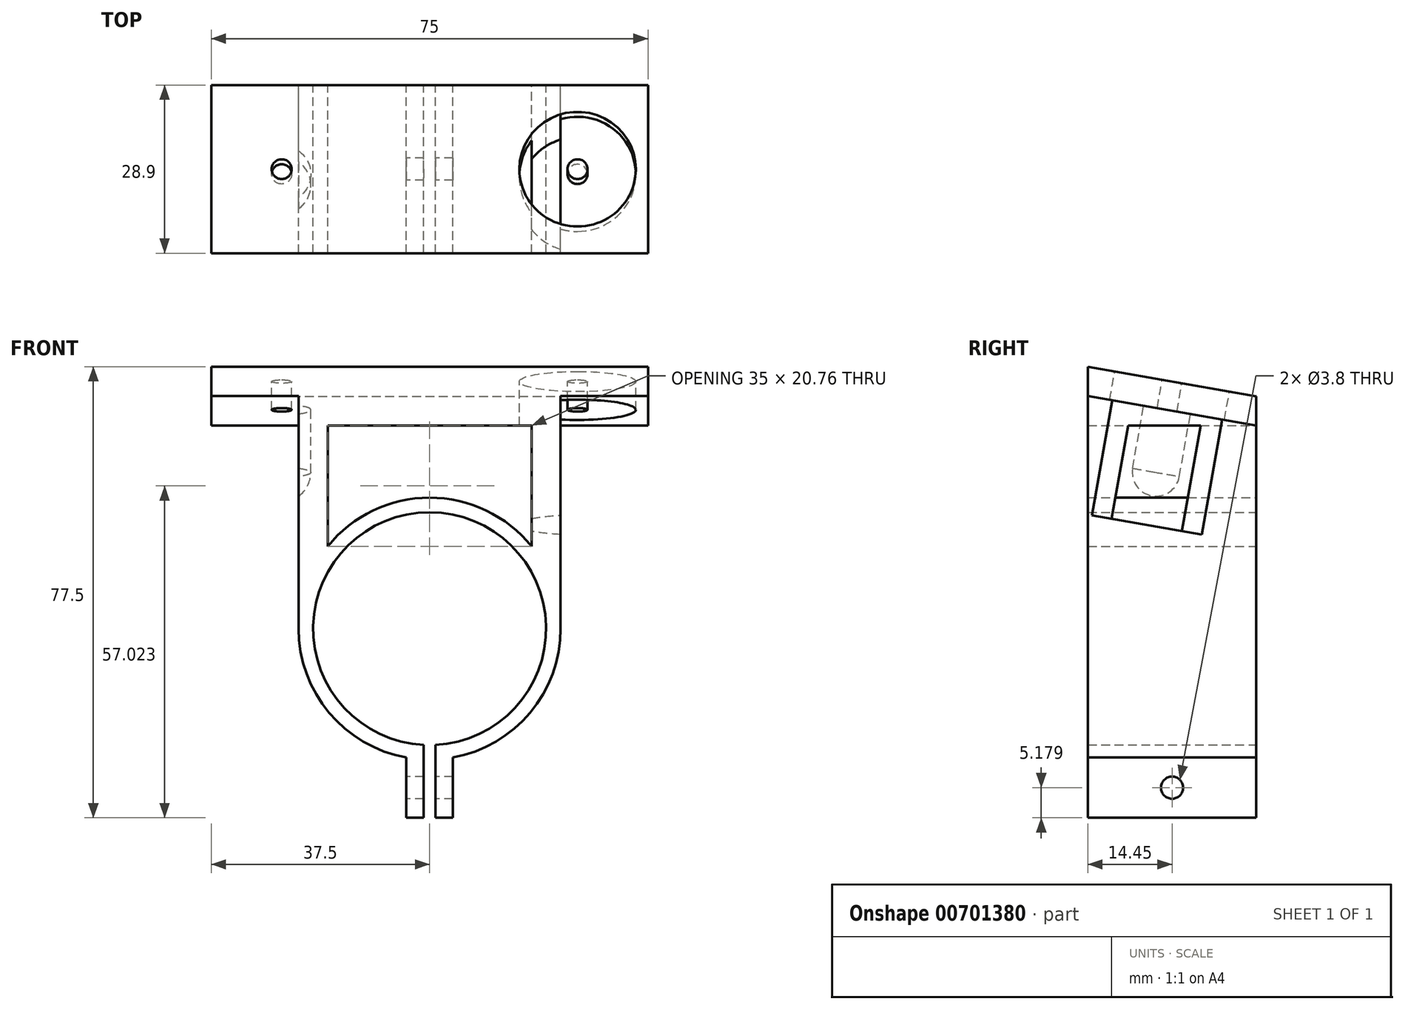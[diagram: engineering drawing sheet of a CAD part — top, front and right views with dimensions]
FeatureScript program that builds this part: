
annotation { "Feature Type Name" : "Feature", "Feature Type Description" : "" }
export const myFeature = defineFeature(function(context is Context, id is Id, definition is map)
    precondition{}
    {
        {
            var Q0;
            Q0=qCreatedBy(makeId("Front.planeOp"),FACE);
            var sketch = newSketch(context, id + "F0", { "sketchPlane" : qUnion([Q0])});
            skCircle(sketch, "E0", {"center": v(0, 0) * mm, "radius": 22.5 * mm});
            skLineSegment(sketch, "E1", {"start": v(-22.5, 0) * mm, "end": v(-22.5, 45) * mm});
            skLineSegment(sketch, "E2", {"start": v(22.5, 0) * mm, "end": v(22.5, 45) * mm});
            skLineSegment(sketch, "E3", {"start": v(22.5, 45) * mm, "end": v(-22.5, 45) * mm});
            skPoint(sketch, "E4", {"position": v(0, -22.5) * mm});
            skSolve(sketch);
        }
        {
            var Q0;
            Q0=makeQuery(id+"F0.imprint","IMPRINT",FACE,{"disambiguationData":[TD([[makeQuery(id+"F0.imprint","IMPRINT",EDGE,{"derivedFrom":sQuery(id+"F0.wireOp",EDGE,"E0")}),1.0]])]});
            var Q1;
            {var subQ0=sQuery(id+"F0.wireOp",EDGE,"E1");Q1=makeQuery(id+"F0.imprint","IMPRINT",FACE,{"disambiguationData":[TD([[makeQuery(id+"F0.imprint","IMPRINT",EDGE,{"derivedFrom":subQ0}),-1.0]])]});}
            extrude(context, id + "F1", {"entities" : qUnion([Q0, Q1]), "depth" : 28.9 * mm, "offsetDistance" : 25 * mm});
        }
        {
            var Q0;
            Q0=sQuery(id+"F0.wireOp",VERTEX,"E0.center");
            var Q1;
            Q1=makeQuery(id+"F1.opExtrude","SWEPT_BODY",BODY,{"disambiguationData":[OSD([sQuery(id+"F0.wireOp",EDGE,"E0")])]});
            hole(context, id + "F2", {"style" : HoleStyle.SIMPLE, "endStyle" : HoleEndStyle.THROUGH, "oppositeDirection" : true, "holeDiameter" : 40 * mm, "majorDiameter" : 5 * mm, "isTappedThrough" : true, "tappedDepth" : 12 * mm, "tapClearance" : 3, "locations" : qUnion([Q0]), "scope" : qUnion([Q1])});
        }
        {
            var Q0;
            Q0=makeQuery(id+"F1.opExtrude","SWEPT_FACE",FACE,{"disambiguationData":[OSD([sQuery(id+"F0.wireOp",EDGE,"E2")])]});
            var sketch = newSketch(context, id + "F3", { "sketchPlane" : qUnion([Q0])});
            skLineSegment(sketch, "E5", {"start": v(-28.9, 45) * mm, "end": v(0, 39.9) * mm});
            skSolve(sketch);
        }
        {
            var Q0;
            {var subQ0=sQuery(id+"F3.wireOp",EDGE,"E5");Q0=makeQuery(id+"F3.imprint","IMPRINT",FACE,{"disambiguationData":[TD([[makeQuery(id+"F3.imprint","IMPRINT",EDGE,{"derivedFrom":subQ0}),1.0]])]});}
            extrude(context, id + "F4", {"entities" : qUnion([Q0]), "operationType" : NewBodyOperationType.REMOVE, "endBound" : BoundingType.THROUGH_ALL, "oppositeDirection" : true, "depth" : 25 * mm, "offsetDistance" : 25 * mm});
        }
        {
            var Q0;
            {var subQ0=sQuery(id+"F0.wireOp",EDGE,"E0");var subQ1=makeQuery(id+"F0.imprint","INTERSECT",VERTEX,{"derivedFrom":[subQ0,sQuery(id+"F0.wireOp",EDGE,"E1")]});Q0=makeQuery(id+"F0.imprint","IMPRINT",FACE,{"disambiguationData":[TD([[makeQuery(id+"F0.imprint","IMPRINT",EDGE,{"disambiguationData":[TD([[subQ1,1.0]])],"derivedFrom":subQ0}),1.0]])]});}
            var sketch = newSketch(context, id + "F5", { "sketchPlane" : qUnion([Q0])});
            skLineSegment(sketch, "E6", {"start": v(0, -24.67) * mm, "end": v(0, 0) * mm, "construction": true});
            skLineSegment(sketch, "E7", {"start": v(1, 7.5) * mm, "end": v(1, 0.8) * mm});
            skLineSegment(sketch, "E8.MirrorCS", {"start": v(-1, 7.5) * mm, "end": v(-1, 0.8) * mm});
            skLineSegment(sketch, "E9.bottom", {"start": v(1, 0.8) * mm, "end": v(-1, 0.8) * mm});
            skLineSegment(sketch, "E9.top", {"start": v(1, -32.5) * mm, "end": v(-1, -32.5) * mm});
            skLineSegment(sketch, "E9.left", {"start": v(1, 0.8) * mm, "end": v(1, -32.5) * mm});
            skLineSegment(sketch, "E9.right", {"start": v(-1, 0.8) * mm, "end": v(-1, -32.5) * mm});
            skLineSegment(sketch, "E10.bottom", {"start": v(-1, 7.5) * mm, "end": v(-4, 7.5) * mm});
            skLineSegment(sketch, "E10.top", {"start": v(-1, -32.5) * mm, "end": v(-4, -32.5) * mm});
            skLineSegment(sketch, "E10.left", {"start": v(-1, 7.5) * mm, "end": v(-1, -32.5) * mm});
            skLineSegment(sketch, "E10.right", {"start": v(-4, 7.5) * mm, "end": v(-4, -32.5) * mm});
            skLineSegment(sketch, "E11.MirrorCS", {"start": v(4, 7.5) * mm, "end": v(4, -32.5) * mm});
            skLineSegment(sketch, "E12.MirrorCS", {"start": v(1, 7.5) * mm, "end": v(4, 7.5) * mm});
            skLineSegment(sketch, "E13.MirrorCS", {"start": v(1, -32.5) * mm, "end": v(4, -32.5) * mm});
            skSolve(sketch);
        }
        {
            var Q0;
            {var subQ0=sQuery(id+"F5.wireOp",EDGE,"E13.MirrorCS");Q0=makeQuery(id+"F5.imprint","IMPRINT",FACE,{"disambiguationData":[TD([[makeQuery(id+"F5.imprint","IMPRINT",EDGE,{"derivedFrom":subQ0}),1.0]])]});}
            var Q1;
            {var subQ0=sQuery(id+"F5.wireOp",EDGE,"E10.top");Q1=makeQuery(id+"F5.imprint","IMPRINT",FACE,{"disambiguationData":[TD([[makeQuery(id+"F5.imprint","IMPRINT",EDGE,{"derivedFrom":subQ0}),-1.0]])]});}
            extrude(context, id + "F6", {"entities" : qUnion([Q0, Q1]), "operationType" : NewBodyOperationType.ADD, "depth" : 28.9 * mm, "offsetDistance" : 25 * mm});
        }
        {
            var Q0;
            {var subQ0=sQuery(id+"F5.wireOp",EDGE,"E9.bottom");Q0=makeQuery(id+"F5.imprint","IMPRINT",FACE,{"disambiguationData":[TD([[makeQuery(id+"F5.imprint","IMPRINT",EDGE,{"derivedFrom":subQ0}),1.0]])]});}
            extrude(context, id + "F7", {"entities" : qUnion([Q0]), "operationType" : NewBodyOperationType.REMOVE, "endBound" : BoundingType.THROUGH_ALL, "depth" : 25 * mm, "offsetDistance" : 25 * mm});
        }
        {
            var Q0;
            Q0=makeQuery(id+"F6.opExtrude","SWEPT_FACE",FACE,{"disambiguationData":[OSD([sQuery(id+"F5.wireOp",EDGE,"E10.right")])]});
            var sketch = newSketch(context, id + "F8", { "sketchPlane" : qUnion([Q0])});
            skLineSegment(sketch, "E14", {"start": v(14.45, -22.14) * mm, "end": v(14.45, -32.5) * mm, "construction": true});
            skCircle(sketch, "E15", {"center": v(14.45, -27.32) * mm, "radius": 1.9 * mm});
            skSolve(sketch);
        }
        {
            var Q0;
            Q0=makeQuery(id+"F8.imprint","IMPRINT",FACE,{"disambiguationData":[TD([[makeQuery(id+"F8.imprint","IMPRINT",EDGE,{"derivedFrom":sQuery(id+"F8.wireOp",EDGE,"E15")}),1.0]])]});
            extrude(context, id + "F9", {"entities" : qUnion([Q0]), "operationType" : NewBodyOperationType.REMOVE, "endBound" : BoundingType.THROUGH_ALL, "oppositeDirection" : true, "depth" : 25 * mm, "offsetDistance" : 25 * mm});
        }
        {
            var Q0;
            Q0=makeQuery(id+"F1.opExtrude","SWEPT_FACE",FACE,{"disambiguationData":[OSD([sQuery(id+"F0.wireOp",EDGE,"E1")])]});
            var sketch = newSketch(context, id + "F10", { "sketchPlane" : qUnion([Q0])});
            skLineSegment(sketch, "E16", {"start": v(0, 39.9) * mm, "end": v(28.9, 45) * mm});
            skLineSegment(sketch, "E17", {"start": v(28.9, 45) * mm, "end": v(28.9, 40) * mm});
            skLineSegment(sketch, "E18", {"start": v(0, 39.9) * mm, "end": v(0, 34.9) * mm});
            skLineSegment(sketch, "E19", {"start": v(28.9, 40) * mm, "end": v(0, 34.9) * mm});
            skSolve(sketch);
        }
        {
            var Q0;
            Q0=makeQuery(id+"F10.imprint","IMPRINT",FACE,{"disambiguationData":[TD([[makeQuery(id+"F10.imprint","IMPRINT",EDGE,{"derivedFrom":sQuery(id+"F10.wireOp",EDGE,"E16")}),-1.0]])]});
            extrude(context, id + "F11", {"entities" : qUnion([Q0]), "operationType" : NewBodyOperationType.ADD, "depth" : 15 * mm, "offsetDistance" : 25 * mm});
        }
        {
            var Q0;
            Q0=makeQuery(id+"F11.opExtrude","CAP_FACE",FACE,{"disambiguationData":[OSD([sQuery(id+"F10.wireOp",EDGE,"E16"),sQuery(id+"F10.wireOp",EDGE,"E17"),sQuery(id+"F10.wireOp",EDGE,"E18"),sQuery(id+"F10.wireOp",EDGE,"E19")])],"isStart":false});
            var sketch = newSketch(context, id + "F12", { "sketchPlane" : qUnion([Q0])});
            skSolve(sketch);
        }
        {
            var Q0;
            Q0=makeQuery(id+"F12.imprint","IMPRINT",FACE,{"disambiguationData":[TD([[makeQuery(id+"F12.imprint","IMPRINT",EDGE,{"derivedFrom":makeQuery(id+"F11.opExtrude","CAP_EDGE",EDGE,{"disambiguationData":[OSD([sQuery(id+"F10.wireOp",EDGE,"E16")])],"isStart":false})}),-1.0]])]});
            extrude(context, id + "F13", {"entities" : qUnion([Q0]), "operationType" : NewBodyOperationType.ADD, "oppositeDirection" : true, "depth" : 75 * mm, "offsetDistance" : 25 * mm});
        }
        {
            var Q0;
            {var subQ0=sQuery(id+"F10.wireOp",EDGE,"E16");Q0=makeQuery(id+"F13.boolean.opBoolean","MERGE",FACE,{"derivedFrom":[makeQuery(id+"F11.boolean.opBoolean","MERGE",FACE,{"derivedFrom":[makeQuery(id+"F4.boolean.opBoolean","COPY",FACE,{"derivedFrom":makeQuery(id+"F4.opExtrude","SWEPT_FACE",FACE,{"disambiguationData":[OSD([sQuery(id+"F3.wireOp",EDGE,"E5")])]})}),makeQuery(id+"F11.opExtrude","SWEPT_FACE",FACE,{"disambiguationData":[OSD([subQ0])]})]}),makeQuery(id+"F13.opExtrude","SWEPT_FACE",FACE,{"disambiguationData":[OSD([subQ0])]})]});}
            var sketch = newSketch(context, id + "F14", { "sketchPlane" : qUnion([Q0])});
            skLineSegment(sketch, "E20", {"start": v(37.5, -21.6) * mm, "end": v(-37.5, -21.6) * mm, "construction": true});
            skLineSegment(sketch, "E21", {"start": v(0, -6.93) * mm, "end": v(0, -36.28) * mm, "construction": true});
            skCircle(sketch, "E22", {"center": v(-25.4, -21.6) * mm, "radius": 1.73 * mm});
            skCircle(sketch, "E23.MirrorC", {"center": v(25.4, -21.6) * mm, "radius": 1.73 * mm});
            skCircle(sketch, "E24", {"center": v(25.4, -21.6) * mm, "radius": 10 * mm});
            skSolve(sketch);
        }
        {
            var Q0;
            Q0=makeQuery(id+"F14.imprint","IMPRINT",FACE,{"disambiguationData":[TD([[makeQuery(id+"F14.imprint","IMPRINT",EDGE,{"derivedFrom":sQuery(id+"F14.wireOp",EDGE,"E22")}),1.0]])]});
            var Q1;
            Q1=makeQuery(id+"F14.imprint","IMPRINT",FACE,{"disambiguationData":[TD([[makeQuery(id+"F14.imprint","IMPRINT",EDGE,{"derivedFrom":sQuery(id+"F14.wireOp",EDGE,"E23.MirrorC")}),-1.0]])]});
            extrude(context, id + "F15", {"entities" : qUnion([Q0, Q1]), "operationType" : NewBodyOperationType.REMOVE, "oppositeDirection" : true, "depth" : 25 * mm, "offsetDistance" : 25 * mm});
        }
        {
            var Q0;
            {var subQ0=sQuery(id+"F10.wireOp",EDGE,"E18");var subQ1=sQuery(id+"F0.wireOp",EDGE,"E0");Q0=makeQuery(id+"F13.boolean.opBoolean","MERGE",FACE,{"derivedFrom":[makeQuery(id+"F11.boolean.opBoolean","MERGE",FACE,{"derivedFrom":[makeQuery(id+"F6.boolean.opBoolean","MERGE",FACE,{"derivedFrom":[makeQuery(id+"F1.opExtrude","CAP_FACE",FACE,{"disambiguationData":[OSD([subQ1,sQuery(id+"F0.wireOp",EDGE,"E1"),sQuery(id+"F0.wireOp",EDGE,"E2"),sQuery(id+"F0.wireOp",EDGE,"E3")])],"isStart":true}),makeQuery(id+"F6.opExtrude","CAP_FACE",FACE,{"disambiguationData":[OSD([subQ1,sQuery(id+"F5.wireOp",EDGE,"E9.left"),sQuery(id+"F5.wireOp",EDGE,"E11.MirrorCS"),sQuery(id+"F5.wireOp",EDGE,"E13.MirrorCS")])],"isStart":true}),makeQuery(id+"F6.opExtrude","CAP_FACE",FACE,{"disambiguationData":[OSD([subQ1,sQuery(id+"F5.wireOp",EDGE,"E10.top"),sQuery(id+"F5.wireOp",EDGE,"E10.left"),sQuery(id+"F5.wireOp",EDGE,"E10.right")])],"isStart":true})]}),makeQuery(id+"F11.opExtrude","SWEPT_FACE",FACE,{"disambiguationData":[OSD([subQ0])]})]}),makeQuery(id+"F13.opExtrude","SWEPT_FACE",FACE,{"disambiguationData":[OSD([subQ0])]})]});}
            var sketch = newSketch(context, id + "F16", { "sketchPlane" : qUnion([Q0])});
            skLineSegment(sketch, "E25", {"start": v(17.5, 34.9) * mm, "end": v(-17.5, 34.9) * mm});
            skLineSegment(sketch, "E26", {"start": v(-17.5, 34.9) * mm, "end": v(-17.5, 14.14) * mm});
            skArc(sketch, "E27", {"start": v(17.5, 14.14) * mm, "mid": v(0, 22.5) * mm, "end": v(-17.5, 14.14) * mm});
            skLineSegment(sketch, "E28", {"start": v(17.5, 34.9) * mm, "end": v(17.5, 14.14) * mm});
            skLineSegment(sketch, "E29", {"start": v(0, 0) * mm, "end": v(0, 46.66) * mm, "construction": true});
            skPoint(sketch, "E29.endSnap0", {"position": v(0, 39.9) * mm});
            skSolve(sketch);
        }
        {
            var Q0;
            Q0=makeQuery(id+"F16.imprint","IMPRINT",FACE,{"disambiguationData":[TD([[makeQuery(id+"F16.imprint","IMPRINT",EDGE,{"derivedFrom":sQuery(id+"F16.wireOp",EDGE,"E25")}),1.0]])]});
            extrude(context, id + "F17", {"entities" : qUnion([Q0]), "operationType" : NewBodyOperationType.REMOVE, "endBound" : BoundingType.THROUGH_ALL, "oppositeDirection" : true, "depth" : 25 * mm, "offsetDistance" : 25 * mm});
        }
        {
            var Q0;
            Q0=makeQuery(id+"F13.opExtrude","SWEPT_FACE",FACE,{"disambiguationData":[OSD([sQuery(id+"F10.wireOp",EDGE,"E19")])]});
            var sketch = newSketch(context, id + "F18", { "sketchPlane" : qUnion([Q0])});
            skPoint(sketch, "E30", {"position": v(25.4, 21.6) * mm});
            skCircle(sketch, "E31", {"center": v(25.4, 21.6) * mm, "radius": 5 * mm});
            skSolve(sketch);
        }
        {
            var Q0;
            Q0 = qSketchRegion(id + "F18", true);
            extrude(context, id + "F19", {"entities" : qUnion([Q0]), "operationType" : NewBodyOperationType.REMOVE, "depth" : 16.1 * mm, "offsetDistance" : 25 * mm});
        }
        {
            var Q0;
            Q0=makeQuery(id+"F11.opExtrude","SWEPT_FACE",FACE,{"disambiguationData":[OSD([sQuery(id+"F10.wireOp",EDGE,"E19")])]});
            var sketch = newSketch(context, id + "F20", { "sketchPlane" : qUnion([Q0])});
            skCircle(sketch, "E32", {"center": v(-25.4, 21.6) * mm, "radius": 5 * mm});
            skSolve(sketch);
        }
        {
            var Q0;
            Q0 = qSketchRegion(id + "F20", true);
            extrude(context, id + "F21", {"entities" : qUnion([Q0]), "operationType" : NewBodyOperationType.REMOVE, "depth" : 15 * mm, "offsetDistance" : 25 * mm});
        }
        {
            var Q0;
            Q0=makeQuery(id+"F19.boolean.opBoolean","COPY",EDGE,{"derivedFrom":makeQuery(id+"F19.opExtrude","CAP_EDGE",EDGE,{"disambiguationData":[OSD([sQuery(id+"F18.wireOp",EDGE,"E31")])],"isStart":false})});
            var Q1;
            Q1=makeQuery(id+"F21.boolean.opBoolean","COPY",EDGE,{"derivedFrom":makeQuery(id+"F21.opExtrude","CAP_EDGE",EDGE,{"disambiguationData":[OSD([sQuery(id+"F20.wireOp",EDGE,"E32")])],"isStart":false})});
            fillet(context, id + "F22", {"entities" : qUnion([Q0, Q1]), "radius" : 5 * mm, "tangentPropagation" : true, "allowEdgeOverflow" : false});
        }
    });
